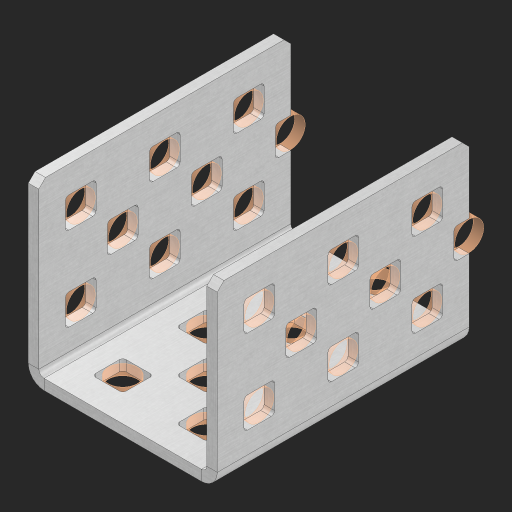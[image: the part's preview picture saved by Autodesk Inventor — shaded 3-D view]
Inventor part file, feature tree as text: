
AUTODESK INVENTOR PART (.ipt)
format: ipt  version: 2023 (Build 270158000, 158)  size: 771,584 bytes
history: native  units: in
note: dims shown in document units (in); Inventor stores cm internally (conversion verified against a paired STEP export)
features: other x42, extrude x34, sheet_metal_op x8, sketch x7, mirror x3, pattern_linear x2, chamfer x1
ambient origin geometry x8: Origin, YZ Plane, XZ Plane, XY Plane, X Axis, Y Axis, Z Axis, Center Point
bodies: Solid1 (feature_tree), Body (feature_tree)
feature tree (97):
  sheet_metal_op  "Flanges"
  sheet_metal_op  "Body Pattern"
  pattern_linear  "Center Pattern"  Spacing1=1.0in  [1 undecoded]
  other  "Arc Length"
  mirror  "Notch Mirror"
  pattern_linear  "Notch Pattern"  Spacing1=0.25in  [1 undecoded]
  other  "Diagonal Plane"
  mirror  "Flange 1"
  mirror  "Flange 2"
  chamfer  "End Chamfer"
  sketch  "Sketch1"  dims[d0=1.0in]
  other  "Plate1"
  sketch  "Sketch2"  dims[d1=1.5in]
  other  "Plate2"
  sheet_metal_op  "Bend1"
  sheet_metal_op  "Corner1"
  sketch  "Sketch8"  dims[d2=0.0625in]
  sketch  "Sketch9"  dims[d3=0.0625in]
  other  "Srf91"
  sheet_metal_op  "Body Pattern Sketch"
  other  "Srf92"
  sketch  "Sketch13"  dims[d4=0.0312in]
  sketch  "Sketch15"  dims[d5=0.125in]
  sketch  "Sketch16"  dims[d6=0.0625in d7=1.0in d8=90.0deg d9=0.0312in d10=0.25in d11=0.0625in d12=0.0625in d49=0.182in d50=0.02in d52=0.25in d53=0.0625in d54=0.0in d55=0.172in d56=1.0in d57=0.0in d60=1.1811in d62=0.5in d63=0.7874in d65=0.5in d85=0.1473in d86=0.1782in d88=0.04in d89=0.0625in d90=0.0in d91=0.04in d92=0.0491in d95=2.5in d96=0.04in d97=0.25in d98=45.0deg d99=0.25in d102=2.497in d106=0.182in d107=0.02in d108=0.5in d110=0.0625in d111=0.0in d112=0.172in d113=0.5in d114=0.0in d117=0.5in d118=0.5in d131=0.25in d132=0.25in]
  other  "Srf786"
  other  "Srf889"
  other  "Srf890"
  other  "Srf1315"
  other  "Srf1316"
  other  "Srf1317"
  other  "Srf1325"
  other  "Srf1326"
  other  "Srf1374"
  other  "Srf1375"
  other  "Srf1376"
  other  "Srf1384"
  other  "Srf1385"
  other  "Srf1433"
  other  "Srf1434"
  other  "Srf1473"
  other  "Srf1474"
  other  "Srf1475"
  other  "Srf1500"
  other  "Srf1501"
  other  "Srf1502"
  other  "Srf1503"
  other  "Srf1538"
  other  "Srf1539"
  other  "Srf1540"
  other  "Srf1541"
  other  "Srf1576"
  other  "Srf1577"
  other  "Srf1578"
  other  "Srf1579"
  other  "Srf1614"
  other  "Srf1615"
  other  "Srf1616"
  other  "Srf1617"
  sheet_metal_op  "Body Stamp"
  sheet_metal_op  "Body Circle"
  other  "Center Stamp"
  other  "Center Circle"
  sheet_metal_op  "Notch"
  extrude  "ExtrusionSrf92"  Depth=0.0625in
  extrude  "ExtrusionSrf889"  Depth=0.0625in
  extrude  "ExtrusionSrf890"  Depth=0.182in
  extrude  "ExtrusionSrf1315"  Depth=0.02in
  extrude  "ExtrusionSrf1316"  Depth=0.25in
  extrude  "ExtrusionSrf1355"  Depth=0.0625in
  extrude  "ExtrusionSrf1356"  TaperAngle=0.0deg  [1 undecoded]
  extrude  "ExtrusionSrf1357"  Depth=0.25in
  extrude  "ExtrusionSrf1374"  Depth=1.0in TaperAngle=0.0deg
  extrude  "ExtrusionSrf1375"  Depth=0.25in
  extrude  "ExtrusionSrf1414"  Depth=0.5in
  extrude  "ExtrusionSrf1415"  Depth=0.25in
  extrude  "ExtrusionSrf1416"  Depth=0.25in
  extrude  "ExtrusionSrf1433"  Depth=0.25in
  extrude  "ExtrusionSrf1434"  Depth=0.0625in
  extrude  "ExtrusionSrf1473"  TaperAngle=0.0deg  [1 undecoded]
  extrude  "ExtrusionSrf1474"  Depth=0.25in
  extrude  "ExtrusionSrf1475"  Depth=0.25in
  extrude  "ExtrusionSrf1500"  Depth=0.25in
  extrude  "ExtrusionSrf1501"  Depth=0.25in TaperAngle=45.0deg
  extrude  "ExtrusionSrf1502"  Depth=0.25in
  extrude  "ExtrusionSrf1503"  Depth=0.25in
  extrude  "ExtrusionSrf1538"  Depth=0.182in
  extrude  "ExtrusionSrf1539"  Depth=0.02in
  extrude  "ExtrusionSrf1540"  Depth=0.5in
  extrude  "ExtrusionSrf1541"  Depth=0.0625in
  extrude  "ExtrusionSrf1576"  TaperAngle=0.0deg  [1 undecoded]
  extrude  "ExtrusionSrf1577"  Depth=0.25in
  extrude  "ExtrusionSrf1578"  Depth=0.5in TaperAngle=0.0deg
  extrude  "ExtrusionSrf1579"  Depth=0.5in
  extrude  "ExtrusionSrf1614"  Depth=0.5in
  extrude  "ExtrusionSrf1615"  Depth=0.25in
  extrude  "ExtrusionSrf1616"  Depth=0.25in
  extrude  "ExtrusionSrf1617"  [1 undecoded]
note: 6 required parameter values undecoded (feature->parameter linkage not recoverable at this tier; creation-order binding heuristic only, values carry confidence <= 0.55)
